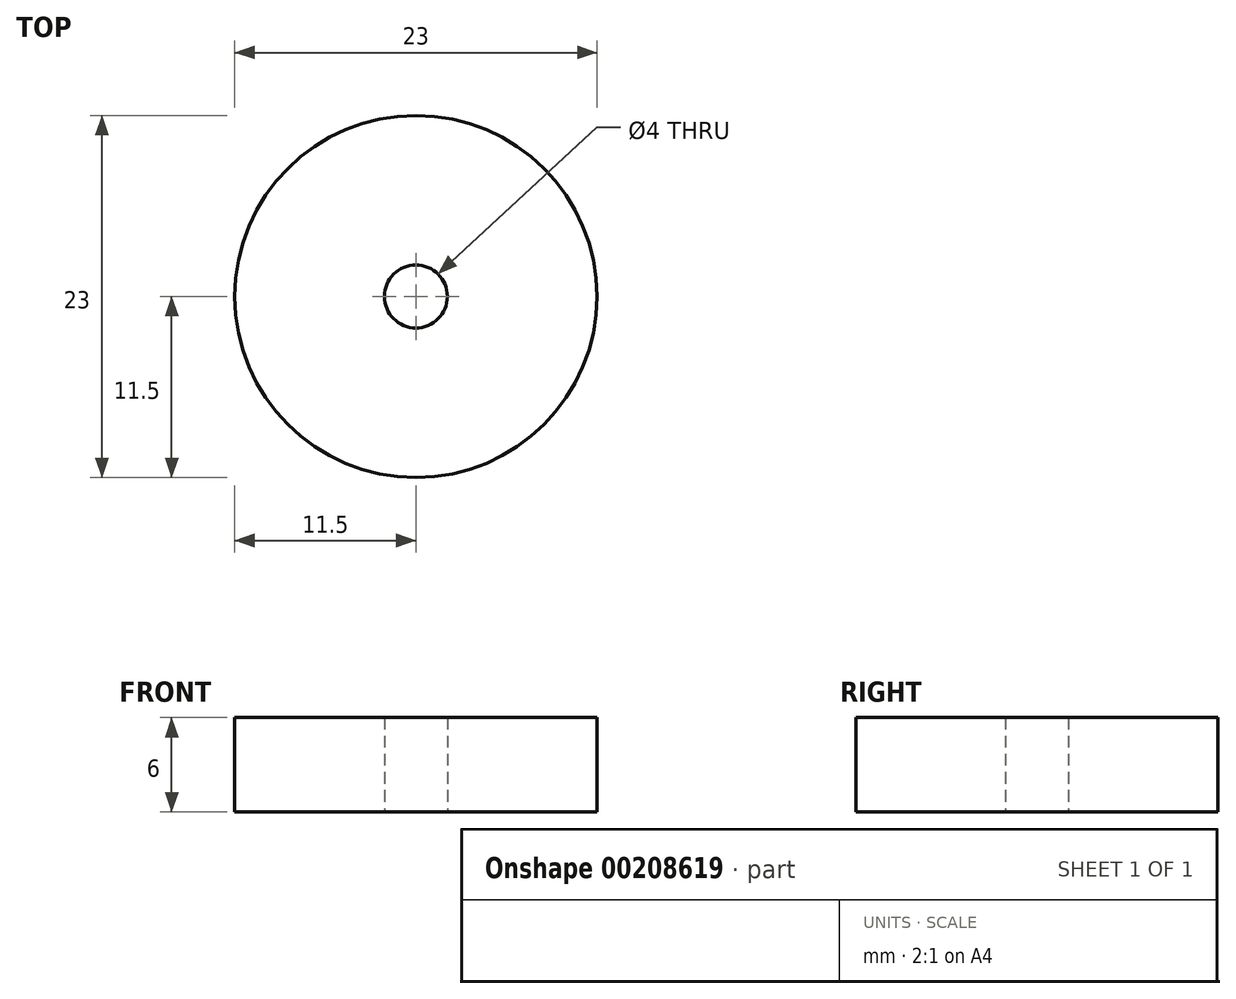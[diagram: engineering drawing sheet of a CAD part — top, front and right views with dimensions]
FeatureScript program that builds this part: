
annotation { "Feature Type Name" : "Feature", "Feature Type Description" : "" }
export const myFeature = defineFeature(function(context is Context, id is Id, definition is map)
    precondition{}
    {
        {
            var Q0;
            Q0=qCreatedBy(makeId("Top.planeOp"),FACE);
            var sketch = newSketch(context, id + "F0", { "sketchPlane" : qUnion([Q0])});
            skCircle(sketch, "E0", {"center": v(0, 0) * mm, "radius": 2 * mm});
            skCircle(sketch, "E1", {"center": v(0, 0) * mm, "radius": 11.5 * mm});
            skSolve(sketch);
        }
        {
            var Q0;
            Q0 = qSketchRegion(id + "F0", true);
            extrude(context, id + "F1", {"entities" : qUnion([Q0]), "depth" : 6 * mm});
        }
        {
            var Q0;
            Q0=qCreatedBy(makeId("Top.planeOp"),FACE);
            var sketch = newSketch(context, id + "F2", { "sketchPlane" : qUnion([Q0])});
            skLineSegment(sketch, "E2.bottom", {"start": v(4, -0.5) * mm, "end": v(-4, -0.5) * mm});
            skLineSegment(sketch, "E2.top", {"start": v(4, 0.5) * mm, "end": v(-4, 0.5) * mm});
            skLineSegment(sketch, "E2.left", {"start": v(4, -0.5) * mm, "end": v(4, 0.5) * mm});
            skLineSegment(sketch, "E2.right", {"start": v(-4, -0.5) * mm, "end": v(-4, 0.5) * mm});
            skPoint(sketch, "E2.middle", {"position": v(0, 0) * mm});
            skSolve(sketch);
        }
        {
            var Q0;
            Q0=qCreatedBy(makeId("Top.planeOp"),FACE);
            var sketch = newSketch(context, id + "F3", { "sketchPlane" : qUnion([Q0])});
            skCircle(sketch, "E3", {"center": v(0, -6) * mm, "radius": 1.5 * mm});
            skSolve(sketch);
        }
        {
            var Q0;
            Q0=qCreatedBy(makeId("Top.planeOp"),FACE);
            var sketch = newSketch(context, id + "F4", { "sketchPlane" : qUnion([Q0])});
            skArc(sketch, "E4", {"start": v(-11.28, 4.1) * mm, "mid": v(2.08, 11.82) * mm, "end": v(12, 0) * mm});
            skArc(sketch, "E5", {"start": v(-8.46, 3.08) * mm, "mid": v(-1.67, 8.84) * mm, "end": v(6.75, 5.95) * mm});
            skLineSegment(sketch, "E6", {"start": v(6.75, 5.95) * mm, "end": v(12, 0) * mm});
            skLineSegment(sketch, "E7", {"start": v(-8.46, 3.08) * mm, "end": v(-11.28, 4.1) * mm});
            skLineSegment(sketch, "E8", {"start": v(0, 0) * mm, "end": v(-5.23, 0) * mm, "construction": true});
            skSolve(sketch);
        }
        {
            var Q0;
            Q0=qCreatedBy(makeId("Top.planeOp"),FACE);
            var sketch = newSketch(context, id + "F5", { "sketchPlane" : qUnion([Q0])});
            skLineSegment(sketch, "E9.bottom", {"start": v(2.99, -2.7) * mm, "end": v(-3.56, 1.88) * mm});
            skLineSegment(sketch, "E9.top", {"start": v(3.56, -1.88) * mm, "end": v(-2.99, 2.7) * mm});
            skLineSegment(sketch, "E9.left", {"start": v(2.99, -2.7) * mm, "end": v(3.56, -1.88) * mm});
            skLineSegment(sketch, "E9.right", {"start": v(-3.56, 1.88) * mm, "end": v(-2.99, 2.7) * mm});
            skPoint(sketch, "E9.middle", {"position": v(0, 0) * mm});
            skLineSegment(sketch, "E10", {"start": v(0, 0) * mm, "end": v(4.88, 0) * mm, "construction": true});
            skCircle(sketch, "E11", {"center": v(-3.44, -4.91) * mm, "radius": 1.5 * mm});
            skLineSegment(sketch, "E12", {"start": v(0, 0) * mm, "end": v(-3.44, -4.91) * mm, "construction": true});
            skSolve(sketch);
        }
    });
